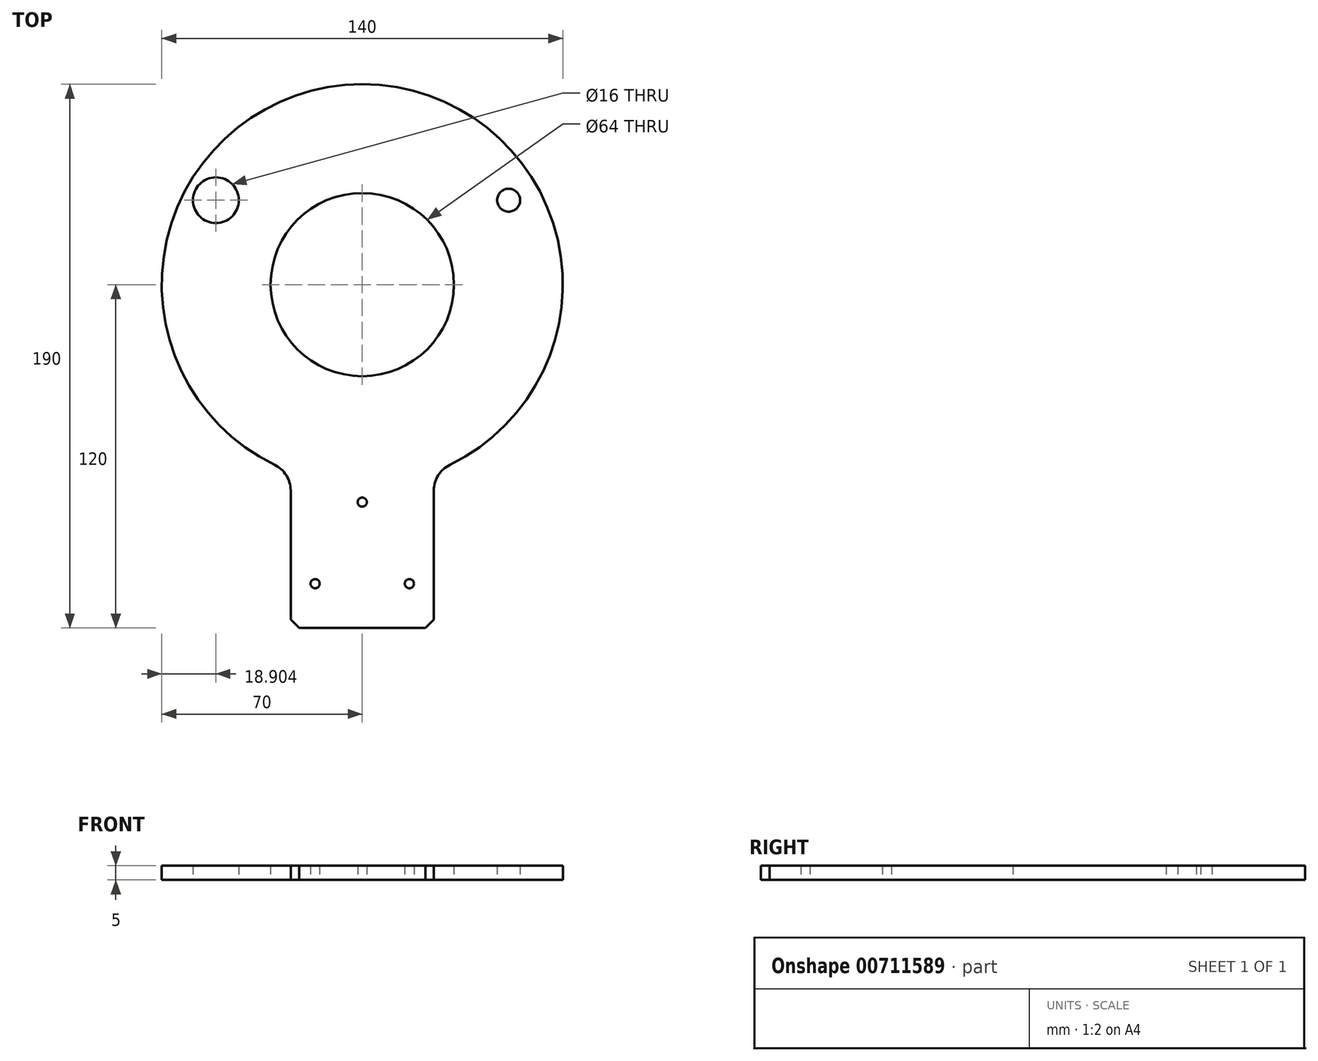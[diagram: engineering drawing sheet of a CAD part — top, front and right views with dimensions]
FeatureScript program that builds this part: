
annotation { "Feature Type Name" : "Feature", "Feature Type Description" : "" }
export const myFeature = defineFeature(function(context is Context, id is Id, definition is map)
    precondition{}
    {
        {
            var Q0;
            Q0=qCreatedBy(makeId("Top.planeOp"),FACE);
            var sketch = newSketch(context, id + "F0", { "sketchPlane" : qUnion([Q0])});
            skArc(sketch, "E0", {"start": v(30.63, -62.95) * mm, "mid": v(0, 70) * mm, "end": v(-30.63, -62.95) * mm, "construction": true});
            skLineSegment(sketch, "E1", {"start": v(25, -71.94) * mm, "end": v(25, -120) * mm});
            skLineSegment(sketch, "E2", {"start": v(25, -120) * mm, "end": v(-25, -120) * mm});
            skLineSegment(sketch, "E3", {"start": v(-25, -120) * mm, "end": v(-25, -71.94) * mm});
            skArc(sketch, "E4", {"start": v(30.62, -62.95) * mm, "mid": v(26.52, -66.63) * mm, "end": v(25, -71.94) * mm});
            skArc(sketch, "E5", {"start": v(-25, -71.94) * mm, "mid": v(-26.52, -66.63) * mm, "end": v(-30.62, -62.95) * mm});
            skArc(sketch, "E6", {"start": v(30.63, -62.95) * mm, "mid": v(0, 70) * mm, "end": v(-30.63, -62.95) * mm});
            skCircle(sketch, "E7", {"center": v(-51.1, 29.5) * mm, "radius": 8 * mm});
            skCircle(sketch, "E8", {"center": v(51.1, 29.5) * mm, "radius": 4 * mm});
            skCircle(sketch, "E9", {"center": v(-16.45, -104.5) * mm, "radius": 1.6 * mm});
            skCircle(sketch, "E10", {"center": v(0, -76) * mm, "radius": 1.6 * mm});
            skCircle(sketch, "E11", {"center": v(16.45, -104.5) * mm, "radius": 1.6 * mm});
            skCircle(sketch, "E12", {"center": v(0, 0) * mm, "radius": 32 * mm});
            skSolve(sketch);
        }
        {
            var Q0;
            Q0 = qSketchRegion(id + "F0", true);
            extrude(context, id + "F1", {"entities" : qUnion([Q0]), "depth" : 5 * mm, "offsetDistance" : 25 * mm});
        }
        {
            var Q0;
            Q0=makeQuery(id+"F1.opExtrude","SWEPT_EDGE",EDGE,{"disambiguationData":[OSD([sQuery(id+"F0.wireOp",EDGE,"E1"),sQuery(id+"F0.wireOp",EDGE,"E2")])]});
            var Q1;
            Q1=makeQuery(id+"F1.opExtrude","SWEPT_EDGE",EDGE,{"disambiguationData":[OSD([sQuery(id+"F0.wireOp",EDGE,"E2"),sQuery(id+"F0.wireOp",EDGE,"E3")])]});
            chamfer(context, id + "F2", {"entities" : qUnion([Q0, Q1]), "width" : 3 * mm, "tangentPropagation" : true});
        }
    });
